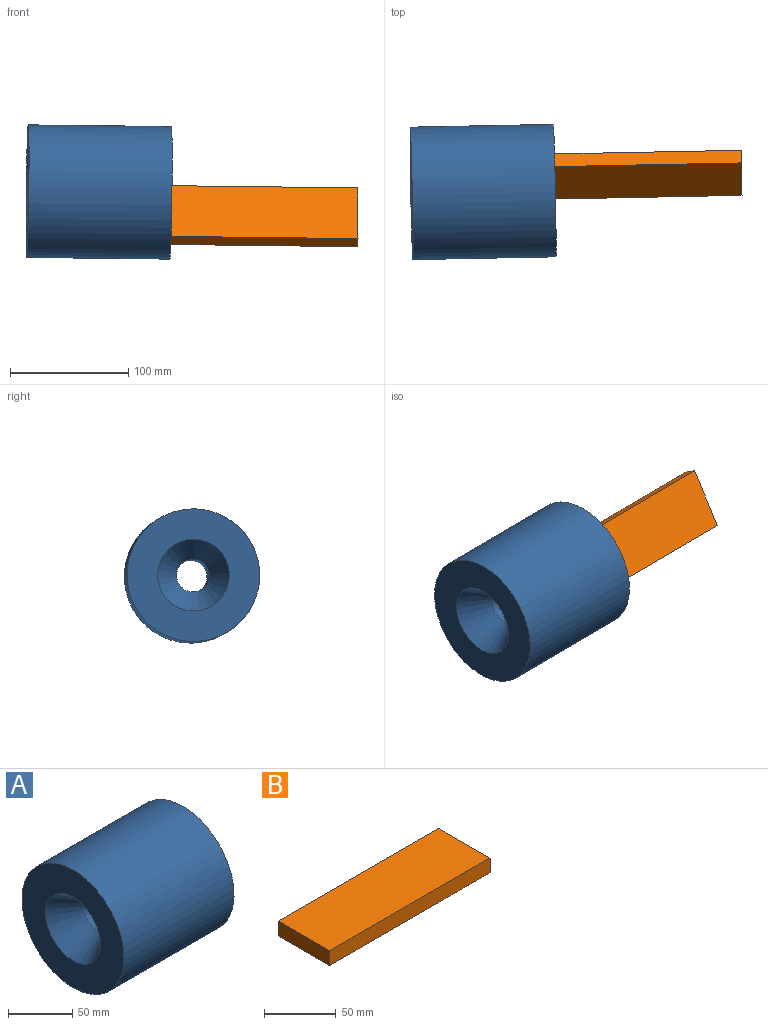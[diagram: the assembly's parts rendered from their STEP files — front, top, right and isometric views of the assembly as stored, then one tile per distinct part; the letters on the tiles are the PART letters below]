
ASSEMBLY  parts=2 mates=1
PART A: 5 faces, bbox 120.9x112.1x112.1 mm
  f0: plane 112.07x112.07mm, normal (1,0,0), area 9264.3mm2, adj f1,f4
  f1: cylinder r=56.03mm len=120.93mm, axis (-1,0,0), area 42574.4mm2, adj f0,f2
  f2: plane 112.07x112.07mm, normal (-1,0,0), area 6979.2mm2, adj f1,f3
  f3: cone r=30.3mm half-angle=32.3deg, axis (-1,0,0), area 4270.8mm2, adj f2,f4
  f4: cylinder r=13.81mm len=94.89mm, axis (-1,0,0), area 8235.6mm2, adj f0,f3
PART B: 6 faces, bbox 158.6x50.8x12.7 mm
  f0: plane 50.8x12.7mm, normal (-1,0,0), area 645.2mm2, adj f1,f3,f4,f5
  f1: plane 158.64x12.7mm, normal (0,-1,0), area 2014.7mm2, adj f0,f2,f4,f5
  f2: plane 50.8x12.7mm, normal (1,0,0), area 645.2mm2, adj f1,f3,f4,f5
  f3: plane 158.64x12.7mm, normal (0,1,0), area 2014.7mm2, adj f0,f2,f4,f5
  f4: plane 158.64x50.8mm, normal (0,0,1), area 8059mm2, adj f0,f1,f2,f3
  f5: plane 158.64x50.8mm, normal (0,0,-1), area 8059mm2, adj f0,f1,f2,f3
PLACE A rot(axis=(1,0.03,0.03),30.1deg) t=(-144.71,-62.44,15.89)mm
PLACE B rot(axis=(1,0.02,0.01),57.5deg) t=(-86.28,-57.58,-28.42)mm
MATE parallel A.f1 <-> B.f0  axis (1,0.02,-0.01) through (-85.7,-61.28,15.2)mm
